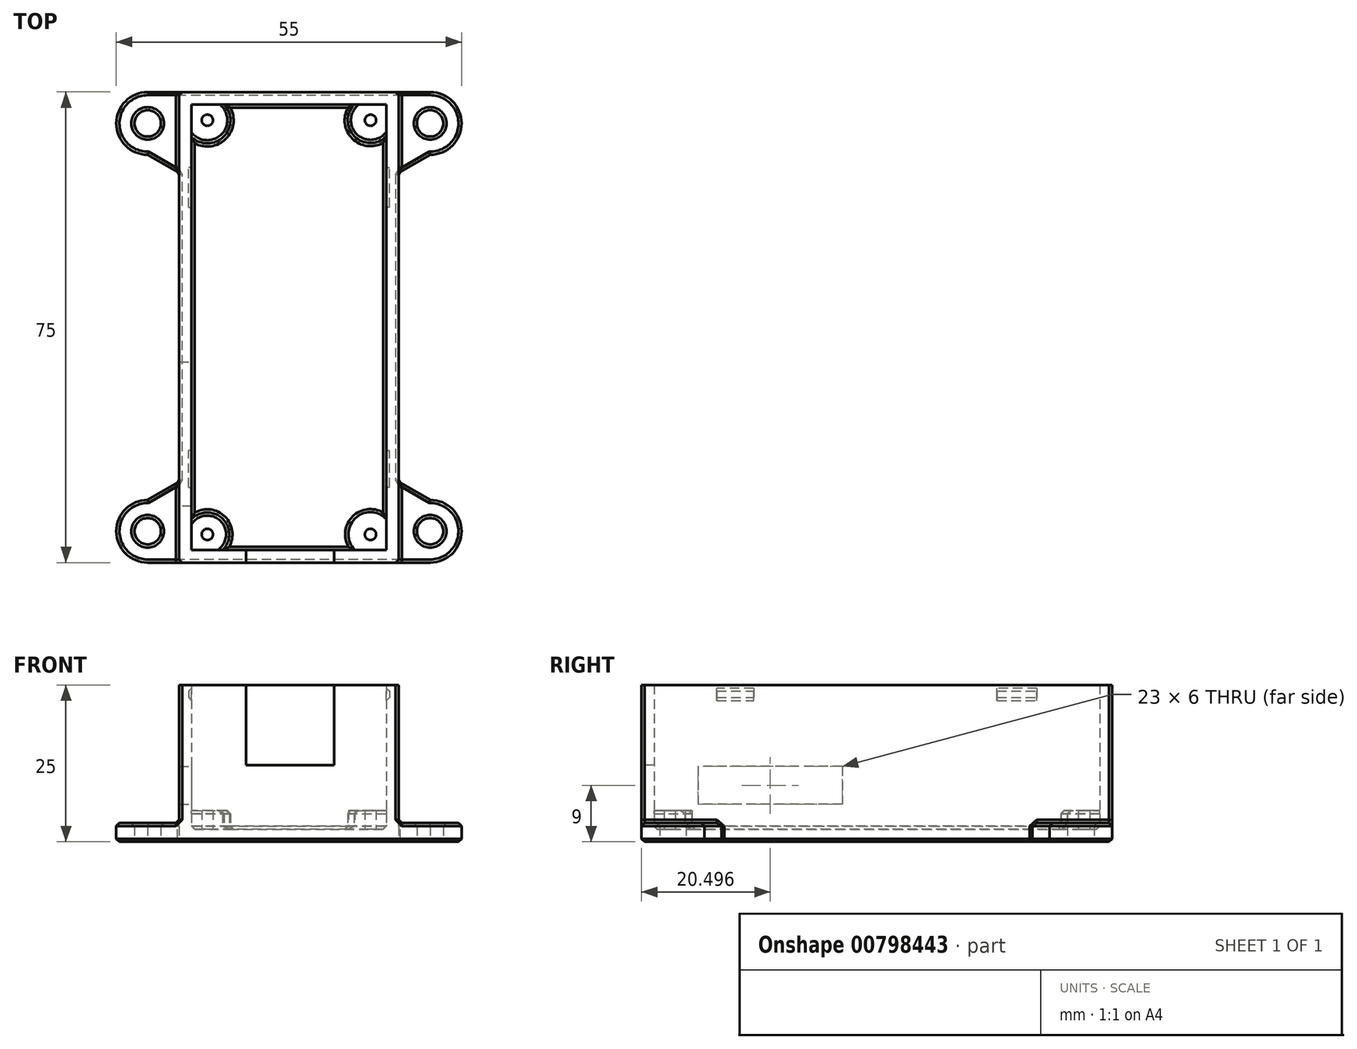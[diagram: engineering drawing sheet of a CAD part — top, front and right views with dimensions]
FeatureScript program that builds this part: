
annotation { "Feature Type Name" : "Feature", "Feature Type Description" : "" }
export const myFeature = defineFeature(function(context is Context, id is Id, definition is map)
    precondition{}
    {
        {
            var Q0;
            Q0=qCreatedBy(makeId("Top.planeOp"),FACE);
            var sketch = newSketch(context, id + "F0", { "sketchPlane" : qUnion([Q0])});
            skLineSegment(sketch, "E0.bottom", {"start": v(-31.58, 41.85) * mm, "end": v(-0.58, 41.85) * mm});
            skLineSegment(sketch, "E0.top", {"start": v(-31.58, -29.15) * mm, "end": v(-0.58, -29.15) * mm});
            skLineSegment(sketch, "E0.left", {"start": v(-31.58, 41.85) * mm, "end": v(-31.58, -29.15) * mm});
            skLineSegment(sketch, "E0.right", {"start": v(-0.58, 41.85) * mm, "end": v(-0.58, -29.15) * mm});
            skCircle(sketch, "E1", {"center": v(-29.08, 39.35) * mm, "radius": 0.9 * mm});
            skCircle(sketch, "E2", {"center": v(-3.08, 39.35) * mm, "radius": 0.9 * mm});
            skCircle(sketch, "E3", {"center": v(-29.08, 39.35) * mm, "radius": 3.69 * mm});
            skCircle(sketch, "E4", {"center": v(-3.08, 39.35) * mm, "radius": 3.62 * mm});
            skCircle(sketch, "E5", {"center": v(-29.08, -26.65) * mm, "radius": 0.9 * mm});
            skCircle(sketch, "E6", {"center": v(-3.08, -26.65) * mm, "radius": 0.9 * mm});
            skCircle(sketch, "E7", {"center": v(-29.08, -26.65) * mm, "radius": 3.5 * mm});
            skCircle(sketch, "E8", {"center": v(-3.08, -26.65) * mm, "radius": 3.54 * mm});
            skLineSegment(sketch, "E9.bottom", {"start": v(-33.58, 43.85) * mm, "end": v(1.42, 43.85) * mm});
            skLineSegment(sketch, "E9.top", {"start": v(-33.58, -31.15) * mm, "end": v(1.42, -31.15) * mm});
            skLineSegment(sketch, "E9.left", {"start": v(-33.58, 43.85) * mm, "end": v(-33.58, -31.15) * mm});
            skLineSegment(sketch, "E9.right", {"start": v(1.42, 43.85) * mm, "end": v(1.42, -31.15) * mm});
            skLineSegment(sketch, "E10.bottom", {"start": v(-32.08, -19.15) * mm, "end": v(-0.08, -19.15) * mm});
            skLineSegment(sketch, "E10.top", {"start": v(-32.08, -13.29) * mm, "end": v(-0.08, -13.29) * mm});
            skLineSegment(sketch, "E10.left", {"start": v(-32.08, -19.15) * mm, "end": v(-32.08, -13.29) * mm});
            skLineSegment(sketch, "E10.right", {"start": v(-0.08, -19.15) * mm, "end": v(-0.08, -13.29) * mm});
            skLineSegment(sketch, "E11.bottom", {"start": v(-32.08, 25.48) * mm, "end": v(-0.08, 25.48) * mm});
            skLineSegment(sketch, "E11.top", {"start": v(-32.08, 31.85) * mm, "end": v(-0.08, 31.85) * mm});
            skLineSegment(sketch, "E11.left", {"start": v(-32.08, 25.48) * mm, "end": v(-32.08, 31.85) * mm});
            skLineSegment(sketch, "E11.right", {"start": v(-0.08, 25.48) * mm, "end": v(-0.08, 31.85) * mm});
            skLineSegment(sketch, "E12.left", {"start": v(-22.9, -29.15) * mm, "end": v(-22.9, -31.15) * mm});
            skLineSegment(sketch, "E12.right", {"start": v(-8.9, -29.15) * mm, "end": v(-8.9, -31.15) * mm});
            skLineSegment(sketch, "E13", {"start": v(1.42, 43.85) * mm, "end": v(6.42, 43.85) * mm});
            skArc(sketch, "E14", {"start": v(6.42, 43.85) * mm, "mid": v(11.42, 38.85) * mm, "end": v(6.42, 33.85) * mm});
            skLineSegment(sketch, "E15", {"start": v(6.42, 33.85) * mm, "end": v(1.42, 30.96) * mm});
            skCircle(sketch, "E16", {"center": v(6.42, 38.85) * mm, "radius": 2.1 * mm});
            skLineSegment(sketch, "E17", {"start": v(-33.58, 43.85) * mm, "end": v(-38.58, 43.85) * mm});
            skArc(sketch, "E18", {"start": v(-38.58, 43.85) * mm, "mid": v(-43.58, 38.85) * mm, "end": v(-38.58, 33.85) * mm});
            skLineSegment(sketch, "E19", {"start": v(-38.58, 33.85) * mm, "end": v(-33.58, 30.96) * mm});
            skLineSegment(sketch, "E20", {"start": v(1.42, -31.15) * mm, "end": v(6.42, -31.15) * mm});
            skArc(sketch, "E21", {"start": v(6.42, -31.15) * mm, "mid": v(11.42, -26.15) * mm, "end": v(6.42, -21.15) * mm});
            skLineSegment(sketch, "E22", {"start": v(6.42, -21.15) * mm, "end": v(1.42, -18.27) * mm});
            skLineSegment(sketch, "E23", {"start": v(-33.58, -31.15) * mm, "end": v(-38.58, -31.15) * mm});
            skArc(sketch, "E24", {"start": v(-38.58, -31.15) * mm, "mid": v(-43.58, -26.15) * mm, "end": v(-38.58, -21.15) * mm});
            skLineSegment(sketch, "E25", {"start": v(-38.58, -21.15) * mm, "end": v(-33.58, -18.27) * mm});
            skCircle(sketch, "E26", {"center": v(-38.58, 38.85) * mm, "radius": 2.1 * mm});
            skCircle(sketch, "E27", {"center": v(-38.58, -26.15) * mm, "radius": 2.1 * mm});
            skCircle(sketch, "E28", {"center": v(6.42, -26.15) * mm, "radius": 2.1 * mm});
            skLineSegment(sketch, "E29", {"start": v(-31.58, -22.15) * mm, "end": v(-33.58, -22.15) * mm});
            skLineSegment(sketch, "E30", {"start": v(-33.58, 0.85) * mm, "end": v(-31.58, 0.85) * mm});
            skSolve(sketch);
        }
        {
            var Q0;
            Q0=makeQuery(id+"F0.imprint","IMPRINT",FACE,{"disambiguationData":[TD([[makeQuery(id+"F0.imprint","IMPRINT",EDGE,{"derivedFrom":sQuery(id+"F0.wireOp",EDGE,"E9.bottom")}),-1.0]])]});
            var Q1;
            {var subQ0=sQuery(id+"F0.wireOp",EDGE,"E0.right");var subQ1=sQuery(id+"F0.wireOp",EDGE,"E0.bottom");var subQ2=makeQuery(id+"F0.imprint","INTERSECT",VERTEX,{"derivedFrom":[subQ1,subQ0]});Q1=makeQuery(id+"F0.imprint","IMPRINT",FACE,{"disambiguationData":[TD([[makeQuery(id+"F0.imprint","IMPRINT",EDGE,{"disambiguationData":[TD([[subQ2,1.0]])],"derivedFrom":subQ1}),1.0]])]});}
            var Q2;
            {var subQ0=sQuery(id+"F0.wireOp",EDGE,"E7");var subQ1=sQuery(id+"F0.wireOp",EDGE,"E0.top");var subQ2=makeQuery(id+"F0.imprint","INTERSECT",VERTEX,{"disambiguationData":[OD(1.0)],"derivedFrom":[subQ1,subQ0]});Q2=makeQuery(id+"F0.imprint","IMPRINT",FACE,{"disambiguationData":[TD([[makeQuery(id+"F0.imprint","IMPRINT",EDGE,{"disambiguationData":[TD([[subQ2,-1.0]])],"derivedFrom":subQ1}),1.0]])]});}
            var Q3;
            {var subQ0=sQuery(id+"F0.wireOp",EDGE,"E12.right");var subQ1=sQuery(id+"F0.wireOp",EDGE,"E0.top");var subQ2=makeQuery(id+"F0.imprint","INTERSECT",VERTEX,{"derivedFrom":[subQ1,subQ0]});Q3=makeQuery(id+"F0.imprint","IMPRINT",FACE,{"disambiguationData":[TD([[makeQuery(id+"F0.imprint","IMPRINT",EDGE,{"disambiguationData":[TD([[subQ2,-1.0]])],"derivedFrom":subQ1}),1.0]])]});}
            var Q4;
            Q4=makeQuery(id+"F0.imprint","IMPRINT",FACE,{"disambiguationData":[TD([[makeQuery(id+"F0.imprint","IMPRINT",EDGE,{"derivedFrom":sQuery(id+"F0.wireOp",EDGE,"E5")}),-1.0]])]});
            var Q5;
            Q5=makeQuery(id+"F0.imprint","IMPRINT",FACE,{"disambiguationData":[TD([[makeQuery(id+"F0.imprint","IMPRINT",EDGE,{"derivedFrom":sQuery(id+"F0.wireOp",EDGE,"E1")}),-1.0]])]});
            var Q6;
            {var subQ0=sQuery(id+"F0.wireOp",EDGE,"E0.left");var subQ1=sQuery(id+"F0.wireOp",EDGE,"E0.bottom");var subQ2=makeQuery(id+"F0.imprint","INTERSECT",VERTEX,{"derivedFrom":[subQ1,subQ0]});Q6=makeQuery(id+"F0.imprint","IMPRINT",FACE,{"disambiguationData":[TD([[makeQuery(id+"F0.imprint","IMPRINT",EDGE,{"disambiguationData":[TD([[subQ2,-1.0]])],"derivedFrom":subQ1}),1.0]])]});}
            var Q7;
            {var subQ0=sQuery(id+"F0.wireOp",EDGE,"E12.left");var subQ1=sQuery(id+"F0.wireOp",EDGE,"E0.top");var subQ2=makeQuery(id+"F0.imprint","INTERSECT",VERTEX,{"derivedFrom":[subQ1,subQ0]});Q7=makeQuery(id+"F0.imprint","IMPRINT",FACE,{"disambiguationData":[TD([[makeQuery(id+"F0.imprint","IMPRINT",EDGE,{"disambiguationData":[TD([[subQ2,-1.0]])],"derivedFrom":subQ1}),-1.0]])]});}
            var Q8;
            {var subQ0=sQuery(id+"F0.wireOp",EDGE,"E11.top");var subQ1=sQuery(id+"F0.wireOp",EDGE,"E0.left");var subQ2=makeQuery(id+"F0.imprint","INTERSECT",VERTEX,{"derivedFrom":[subQ1,subQ0]});Q8=makeQuery(id+"F0.imprint","IMPRINT",FACE,{"disambiguationData":[TD([[makeQuery(id+"F0.imprint","IMPRINT",EDGE,{"disambiguationData":[TD([[subQ2,-1.0]])],"derivedFrom":subQ1}),1.0]])]});}
            var Q9;
            {var subQ3=sQuery(id+"F0.wireOp",EDGE,"E7");var subQ6=sQuery(id+"F0.wireOp",EDGE,"E0.top");var subQ9=makeQuery(id+"F0.imprint","INTERSECT",VERTEX,{"disambiguationData":[OD(1.0)],"derivedFrom":[subQ6,subQ3]});Q9=makeQuery(id+"F0.imprint","IMPRINT",FACE,{"disambiguationData":[TD([[makeQuery(id+"F0.imprint","IMPRINT",EDGE,{"disambiguationData":[TD([[subQ9,-1.0]])],"derivedFrom":subQ6}),-1.0]])]});}
            var Q10;
            Q10=makeQuery(id+"F0.imprint","IMPRINT",FACE,{"disambiguationData":[TD([[makeQuery(id+"F0.imprint","IMPRINT",EDGE,{"derivedFrom":sQuery(id+"F0.wireOp",EDGE,"E2")}),-1.0]])]});
            var Q11;
            {var subQ0=sQuery(id+"F0.wireOp",EDGE,"E10.top");var subQ1=sQuery(id+"F0.wireOp",EDGE,"E0.left");var subQ2=makeQuery(id+"F0.imprint","INTERSECT",VERTEX,{"derivedFrom":[subQ1,subQ0]});Q11=makeQuery(id+"F0.imprint","IMPRINT",FACE,{"disambiguationData":[TD([[makeQuery(id+"F0.imprint","IMPRINT",EDGE,{"disambiguationData":[TD([[subQ2,-1.0]])],"derivedFrom":subQ1}),1.0]])]});}
            var Q12;
            {var subQ5=sQuery(id+"F0.wireOp",EDGE,"E12.bottom");Q12=makeQuery(id+"F0.imprint","IMPRINT",FACE,{"disambiguationData":[TD([[makeQuery(id+"F0.imprint","IMPRINT",EDGE,{"derivedFrom":subQ5}),-1.0]])]});}
            var Q13;
            {var subQ0=sQuery(id+"F0.wireOp",EDGE,"E11.bottom");var subQ1=sQuery(id+"F0.wireOp",EDGE,"E0.left");var subQ2=makeQuery(id+"F0.imprint","INTERSECT",VERTEX,{"derivedFrom":[subQ1,subQ0]});Q13=makeQuery(id+"F0.imprint","IMPRINT",FACE,{"disambiguationData":[TD([[makeQuery(id+"F0.imprint","IMPRINT",EDGE,{"disambiguationData":[TD([[subQ2,-1.0]])],"derivedFrom":subQ1}),1.0]])]});}
            var Q14;
            {var subQ0=sQuery(id+"F0.wireOp",EDGE,"E12.left");var subQ1=sQuery(id+"F0.wireOp",EDGE,"E0.top");var subQ2=makeQuery(id+"F0.imprint","INTERSECT",VERTEX,{"derivedFrom":[subQ1,subQ0]});Q14=makeQuery(id+"F0.imprint","IMPRINT",FACE,{"disambiguationData":[TD([[makeQuery(id+"F0.imprint","IMPRINT",EDGE,{"disambiguationData":[TD([[subQ2,-1.0]])],"derivedFrom":subQ1}),1.0]])]});}
            var Q15;
            Q15=makeQuery(id+"F0.imprint","IMPRINT",FACE,{"disambiguationData":[TD([[makeQuery(id+"F0.imprint","IMPRINT",EDGE,{"derivedFrom":sQuery(id+"F0.wireOp",EDGE,"E6")}),-1.0]])]});
            var Q16;
            {var subQ14=sQuery(id+"F0.wireOp",EDGE,"E12.bottom");Q16=makeQuery(id+"F0.imprint","IMPRINT",FACE,{"disambiguationData":[TD([[makeQuery(id+"F0.imprint","IMPRINT",EDGE,{"derivedFrom":subQ14}),1.0]])]});}
            var Q17;
            {var subQ0=sQuery(id+"F0.wireOp",EDGE,"E3");var subQ1=sQuery(id+"F0.wireOp",EDGE,"E0.bottom");var subQ2=makeQuery(id+"F0.imprint","INTERSECT",VERTEX,{"derivedFrom":[subQ1,subQ0]});Q17=makeQuery(id+"F0.imprint","IMPRINT",FACE,{"disambiguationData":[TD([[makeQuery(id+"F0.imprint","IMPRINT",EDGE,{"disambiguationData":[TD([[subQ2,-1.0]])],"derivedFrom":subQ1}),-1.0]])]});}
            var Q18;
            {var subQ3=sQuery(id+"F0.wireOp",EDGE,"E12.right");var subQ7=sQuery(id+"F0.wireOp",EDGE,"E0.top");var subQ9=makeQuery(id+"F0.imprint","INTERSECT",VERTEX,{"derivedFrom":[subQ7,subQ3]});Q18=makeQuery(id+"F0.imprint","IMPRINT",FACE,{"disambiguationData":[TD([[makeQuery(id+"F0.imprint","IMPRINT",EDGE,{"disambiguationData":[TD([[subQ9,-1.0]])],"derivedFrom":subQ7}),-1.0]])]});}
            var Q19;
            {var subQ0=sQuery(id+"F0.wireOp",EDGE,"E7");var subQ1=sQuery(id+"F0.wireOp",EDGE,"E0.left");var subQ2=makeQuery(id+"F0.imprint","INTERSECT",VERTEX,{"disambiguationData":[OD(0.0)],"derivedFrom":[subQ1,subQ0]});Q19=makeQuery(id+"F0.imprint","IMPRINT",FACE,{"disambiguationData":[TD([[makeQuery(id+"F0.imprint","IMPRINT",EDGE,{"disambiguationData":[TD([[subQ2,-1.0]])],"derivedFrom":subQ1}),-1.0]])]});}
            var Q20;
            {var subQ0=sQuery(id+"F0.wireOp",EDGE,"2mZLKPwa-GTBg-M3pd-c2KF-U8wC3PhsdAiK.left");var subQ1=sQuery(id+"F0.wireOp",EDGE,"E0.top");var subQ2=makeQuery(id+"F0.imprint","INTERSECT",VERTEX,{"derivedFrom":[subQ1,subQ0]});Q20=makeQuery(id+"F0.imprint","IMPRINT",FACE,{"disambiguationData":[TD([[makeQuery(id+"F0.imprint","IMPRINT",EDGE,{"disambiguationData":[TD([[subQ2,-1.0]])],"derivedFrom":subQ1}),1.0]])]});}
            var Q21;
            {var subQ0=sQuery(id+"F0.wireOp",EDGE,"E8");var subQ1=sQuery(id+"F0.wireOp",EDGE,"E0.top");var subQ2=makeQuery(id+"F0.imprint","INTERSECT",VERTEX,{"derivedFrom":[subQ1,subQ0]});Q21=makeQuery(id+"F0.imprint","IMPRINT",FACE,{"disambiguationData":[TD([[makeQuery(id+"F0.imprint","IMPRINT",EDGE,{"disambiguationData":[TD([[subQ2,-1.0]])],"derivedFrom":subQ1}),-1.0]])]});}
            var Q22;
            {var subQ5=sQuery(id+"F0.wireOp",EDGE,"E11.right");Q22=makeQuery(id+"F0.imprint","IMPRINT",FACE,{"disambiguationData":[TD([[makeQuery(id+"F0.imprint","IMPRINT",EDGE,{"derivedFrom":subQ5}),1.0]])]});}
            var Q23;
            {var subQ5=sQuery(id+"F0.wireOp",EDGE,"E10.right");Q23=makeQuery(id+"F0.imprint","IMPRINT",FACE,{"disambiguationData":[TD([[makeQuery(id+"F0.imprint","IMPRINT",EDGE,{"derivedFrom":subQ5}),1.0]])]});}
            var Q24;
            {var subQ5=sQuery(id+"F0.wireOp",EDGE,"E10.left");Q24=makeQuery(id+"F0.imprint","IMPRINT",FACE,{"disambiguationData":[TD([[makeQuery(id+"F0.imprint","IMPRINT",EDGE,{"derivedFrom":subQ5}),-1.0]])]});}
            var Q25;
            {var subQ5=sQuery(id+"F0.wireOp",EDGE,"E11.left");Q25=makeQuery(id+"F0.imprint","IMPRINT",FACE,{"disambiguationData":[TD([[makeQuery(id+"F0.imprint","IMPRINT",EDGE,{"derivedFrom":subQ5}),-1.0]])]});}
            var Q26;
            {var subQ1=sQuery(id+"F0.wireOp",EDGE,"E0.top");var subQ3=sQuery(id+"F0.wireOp",EDGE,"2mZLKPwa-GTBg-M3pd-c2KF-U8wC3PhsdAiK.right");var subQ4=makeQuery(id+"F0.imprint","INTERSECT",VERTEX,{"derivedFrom":[subQ1,subQ3]});Q26=makeQuery(id+"F0.imprint","IMPRINT",FACE,{"disambiguationData":[TD([[makeQuery(id+"F0.imprint","IMPRINT",EDGE,{"disambiguationData":[TD([[subQ4,1.0]])],"derivedFrom":subQ3}),-1.0]])]});}
            var Q27;
            {var subQ0=sQuery(id+"F0.wireOp",EDGE,"E8");var subQ1=sQuery(id+"F0.wireOp",EDGE,"E0.right");var subQ3=makeQuery(id+"F0.imprint","INTERSECT",VERTEX,{"derivedFrom":[subQ1,subQ0]});Q27=makeQuery(id+"F0.imprint","IMPRINT",FACE,{"disambiguationData":[TD([[makeQuery(id+"F0.imprint","IMPRINT",EDGE,{"disambiguationData":[TD([[subQ3,-1.0]])],"derivedFrom":subQ1}),1.0]])]});}
            var Q28;
            {var subQ0=sQuery(id+"F0.wireOp",EDGE,"2mZLKPwa-GTBg-M3pd-c2KF-U8wC3PhsdAiK.left");var subQ1=sQuery(id+"F0.wireOp",EDGE,"E0.top");var subQ2=makeQuery(id+"F0.imprint","INTERSECT",VERTEX,{"derivedFrom":[subQ1,subQ0]});Q28=makeQuery(id+"F0.imprint","IMPRINT",FACE,{"disambiguationData":[TD([[makeQuery(id+"F0.imprint","IMPRINT",EDGE,{"disambiguationData":[TD([[subQ2,-1.0]])],"derivedFrom":subQ1}),-1.0]])]});}
            var Q29;
            {var subQ0=sQuery(id+"F0.wireOp",EDGE,"E8");var subQ1=sQuery(id+"F0.wireOp",EDGE,"E0.top");var subQ2=makeQuery(id+"F0.imprint","INTERSECT",VERTEX,{"derivedFrom":[subQ1,subQ0]});Q29=makeQuery(id+"F0.imprint","IMPRINT",FACE,{"disambiguationData":[TD([[makeQuery(id+"F0.imprint","IMPRINT",EDGE,{"disambiguationData":[TD([[subQ2,-1.0]])],"derivedFrom":subQ1}),1.0]])]});}
            var Q30;
            {var subQ0=sQuery(id+"F0.wireOp",EDGE,"E7");var subQ1=sQuery(id+"F0.wireOp",EDGE,"E0.top");var subQ2=makeQuery(id+"F0.imprint","INTERSECT",VERTEX,{"disambiguationData":[OD(0.0)],"derivedFrom":[subQ1,subQ0]});Q30=makeQuery(id+"F0.imprint","IMPRINT",FACE,{"disambiguationData":[TD([[makeQuery(id+"F0.imprint","IMPRINT",EDGE,{"disambiguationData":[TD([[subQ2,-1.0]])],"derivedFrom":subQ1}),-1.0]])]});}
            var Q31;
            {var subQ0=sQuery(id+"F0.wireOp",EDGE,"E0.left");var subQ1=sQuery(id+"F0.wireOp",EDGE,"E0.top");var subQ2=makeQuery(id+"F0.imprint","INTERSECT",VERTEX,{"derivedFrom":[subQ1,subQ0]});Q31=makeQuery(id+"F0.imprint","IMPRINT",FACE,{"disambiguationData":[TD([[makeQuery(id+"F0.imprint","IMPRINT",EDGE,{"disambiguationData":[TD([[subQ2,-1.0]])],"derivedFrom":subQ1}),1.0]])]});}
            var Q32;
            Q32=makeQuery(id+"F0.imprint","IMPRINT",FACE,{"disambiguationData":[TD([[makeQuery(id+"F0.imprint","IMPRINT",EDGE,{"derivedFrom":sQuery(id+"F0.wireOp",EDGE,"E6")}),1.0]])]});
            var Q33;
            Q33=makeQuery(id+"F0.imprint","IMPRINT",FACE,{"disambiguationData":[TD([[makeQuery(id+"F0.imprint","IMPRINT",EDGE,{"derivedFrom":sQuery(id+"F0.wireOp",EDGE,"E5")}),1.0]])]});
            var Q34;
            Q34=makeQuery(id+"F0.imprint","IMPRINT",FACE,{"disambiguationData":[TD([[makeQuery(id+"F0.imprint","IMPRINT",EDGE,{"derivedFrom":sQuery(id+"F0.wireOp",EDGE,"E2")}),1.0]])]});
            var Q35;
            Q35=makeQuery(id+"F0.imprint","IMPRINT",FACE,{"disambiguationData":[TD([[makeQuery(id+"F0.imprint","IMPRINT",EDGE,{"derivedFrom":sQuery(id+"F0.wireOp",EDGE,"E1")}),1.0]])]});
            var Q36;
            {var subQ0=sQuery(id+"F0.wireOp",EDGE,"2mZLKPwa-GTBg-M3pd-c2KF-U8wC3PhsdAiK.left");var subQ3=sQuery(id+"F0.wireOp",EDGE,"E7");var subQ4=makeQuery(id+"F0.imprint","INTERSECT",VERTEX,{"derivedFrom":[subQ3,subQ0]});Q36=makeQuery(id+"F0.imprint","IMPRINT",FACE,{"disambiguationData":[TD([[makeQuery(id+"F0.imprint","IMPRINT",EDGE,{"disambiguationData":[TD([[subQ4,-1.0]])],"derivedFrom":subQ3}),-1.0]])]});}
            var Q37;
            {var subQ0=sQuery(id+"F0.wireOp",EDGE,"E12.left");var subQ1=sQuery(id+"F0.wireOp",EDGE,"E9.top");var subQ2=makeQuery(id+"F0.imprint","INTERSECT",VERTEX,{"derivedFrom":[subQ1,subQ0]});Q37=makeQuery(id+"F0.imprint","IMPRINT",FACE,{"disambiguationData":[TD([[makeQuery(id+"F0.imprint","IMPRINT",EDGE,{"disambiguationData":[TD([[subQ2,-1.0]])],"derivedFrom":subQ1}),1.0]])]});}
            var Q38;
            {var subQ3=sQuery(id+"F0.wireOp",EDGE,"E8");var subQ7=sQuery(id+"F0.wireOp",EDGE,"2mZLKPwa-GTBg-M3pd-c2KF-U8wC3PhsdAiK.top");var subQ9=makeQuery(id+"F0.imprint","INTERSECT",VERTEX,{"derivedFrom":[subQ3,subQ7]});Q38=makeQuery(id+"F0.imprint","IMPRINT",FACE,{"disambiguationData":[TD([[makeQuery(id+"F0.imprint","IMPRINT",EDGE,{"disambiguationData":[TD([[subQ9,-1.0]])],"derivedFrom":subQ3}),-1.0]])]});}
            var Q39;
            {var subQ0=sQuery(id+"F0.wireOp",EDGE,"2mZLKPwa-GTBg-M3pd-c2KF-U8wC3PhsdAiK.left");var subQ1=sQuery(id+"F0.wireOp",EDGE,"E7");var subQ2=makeQuery(id+"F0.imprint","INTERSECT",VERTEX,{"derivedFrom":[subQ1,subQ0]});Q39=makeQuery(id+"F0.imprint","IMPRINT",FACE,{"disambiguationData":[TD([[makeQuery(id+"F0.imprint","IMPRINT",EDGE,{"disambiguationData":[TD([[subQ2,-1.0]])],"derivedFrom":subQ1}),1.0]])]});}
            var Q40;
            {var subQ0=sQuery(id+"F0.wireOp",EDGE,"2mZLKPwa-GTBg-M3pd-c2KF-U8wC3PhsdAiK.top");var subQ1=sQuery(id+"F0.wireOp",EDGE,"E8");var subQ2=makeQuery(id+"F0.imprint","INTERSECT",VERTEX,{"derivedFrom":[subQ1,subQ0]});Q40=makeQuery(id+"F0.imprint","IMPRINT",FACE,{"disambiguationData":[TD([[makeQuery(id+"F0.imprint","IMPRINT",EDGE,{"disambiguationData":[TD([[subQ2,-1.0]])],"derivedFrom":subQ1}),1.0]])]});}
            var Q41;
            {var subQ7=sQuery(id+"F0.wireOp",EDGE,"E10.left");Q41=makeQuery(id+"F0.imprint","IMPRINT",FACE,{"disambiguationData":[TD([[makeQuery(id+"F0.imprint","IMPRINT",EDGE,{"derivedFrom":subQ7}),1.0]])]});}
            extrude(context, id + "F1", {"entities" : qUnion([Q0, Q1, Q2, Q3, Q4, Q5, Q6, Q7, Q8, Q9, Q10, Q11, Q12, Q13, Q14, Q15, Q16, Q17, Q18, Q19, Q20, Q21, Q22, Q23, Q24, Q25, Q26, Q27, Q28, Q29, Q30, Q31, Q32, Q33, Q34, Q35, Q36, Q37, Q38, Q39, Q40, Q41]), "depth" : 25 * mm, "offsetDistance" : 25 * mm});
        }
        {
            var Q0;
            {var subQ0=sQuery(id+"F0.wireOp",EDGE,"E3");var subQ1=sQuery(id+"F0.wireOp",EDGE,"E0.bottom");var subQ2=makeQuery(id+"F0.imprint","INTERSECT",VERTEX,{"derivedFrom":[subQ1,subQ0]});Q0=makeQuery(id+"F0.imprint","IMPRINT",FACE,{"disambiguationData":[TD([[makeQuery(id+"F0.imprint","IMPRINT",EDGE,{"disambiguationData":[TD([[subQ2,-1.0]])],"derivedFrom":subQ1}),-1.0]])]});}
            var Q1;
            {var subQ0=sQuery(id+"F0.wireOp",EDGE,"E11.top");var subQ1=sQuery(id+"F0.wireOp",EDGE,"E0.left");var subQ2=makeQuery(id+"F0.imprint","INTERSECT",VERTEX,{"derivedFrom":[subQ1,subQ0]});Q1=makeQuery(id+"F0.imprint","IMPRINT",FACE,{"disambiguationData":[TD([[makeQuery(id+"F0.imprint","IMPRINT",EDGE,{"disambiguationData":[TD([[subQ2,-1.0]])],"derivedFrom":subQ1}),1.0]])]});}
            var Q2;
            {var subQ0=sQuery(id+"F0.wireOp",EDGE,"E11.bottom");var subQ1=sQuery(id+"F0.wireOp",EDGE,"E0.left");var subQ2=makeQuery(id+"F0.imprint","INTERSECT",VERTEX,{"derivedFrom":[subQ1,subQ0]});Q2=makeQuery(id+"F0.imprint","IMPRINT",FACE,{"disambiguationData":[TD([[makeQuery(id+"F0.imprint","IMPRINT",EDGE,{"disambiguationData":[TD([[subQ2,-1.0]])],"derivedFrom":subQ1}),1.0]])]});}
            var Q3;
            {var subQ0=sQuery(id+"F0.wireOp",EDGE,"E10.top");var subQ1=sQuery(id+"F0.wireOp",EDGE,"E0.left");var subQ2=makeQuery(id+"F0.imprint","INTERSECT",VERTEX,{"derivedFrom":[subQ1,subQ0]});Q3=makeQuery(id+"F0.imprint","IMPRINT",FACE,{"disambiguationData":[TD([[makeQuery(id+"F0.imprint","IMPRINT",EDGE,{"disambiguationData":[TD([[subQ2,-1.0]])],"derivedFrom":subQ1}),1.0]])]});}
            var Q4;
            {var subQ14=sQuery(id+"F0.wireOp",EDGE,"E12.bottom");Q4=makeQuery(id+"F0.imprint","IMPRINT",FACE,{"disambiguationData":[TD([[makeQuery(id+"F0.imprint","IMPRINT",EDGE,{"derivedFrom":subQ14}),1.0]])]});}
            var Q5;
            {var subQ5=sQuery(id+"F0.wireOp",EDGE,"E12.bottom");Q5=makeQuery(id+"F0.imprint","IMPRINT",FACE,{"disambiguationData":[TD([[makeQuery(id+"F0.imprint","IMPRINT",EDGE,{"derivedFrom":subQ5}),-1.0]])]});}
            var Q6;
            {var subQ0=sQuery(id+"F0.wireOp",EDGE,"E12.left");var subQ1=sQuery(id+"F0.wireOp",EDGE,"E0.top");var subQ2=makeQuery(id+"F0.imprint","INTERSECT",VERTEX,{"derivedFrom":[subQ1,subQ0]});Q6=makeQuery(id+"F0.imprint","IMPRINT",FACE,{"disambiguationData":[TD([[makeQuery(id+"F0.imprint","IMPRINT",EDGE,{"disambiguationData":[TD([[subQ2,-1.0]])],"derivedFrom":subQ1}),1.0]])]});}
            var Q7;
            {var subQ0=sQuery(id+"F0.wireOp",EDGE,"E12.right");var subQ1=sQuery(id+"F0.wireOp",EDGE,"E0.top");var subQ2=makeQuery(id+"F0.imprint","INTERSECT",VERTEX,{"derivedFrom":[subQ1,subQ0]});Q7=makeQuery(id+"F0.imprint","IMPRINT",FACE,{"disambiguationData":[TD([[makeQuery(id+"F0.imprint","IMPRINT",EDGE,{"disambiguationData":[TD([[subQ2,-1.0]])],"derivedFrom":subQ1}),1.0]])]});}
            var Q8;
            Q8=makeQuery(id+"F0.imprint","IMPRINT",FACE,{"disambiguationData":[TD([[makeQuery(id+"F0.imprint","IMPRINT",EDGE,{"derivedFrom":sQuery(id+"F0.wireOp",EDGE,"E6")}),1.0]])]});
            var Q9;
            Q9=makeQuery(id+"F0.imprint","IMPRINT",FACE,{"disambiguationData":[TD([[makeQuery(id+"F0.imprint","IMPRINT",EDGE,{"derivedFrom":sQuery(id+"F0.wireOp",EDGE,"E5")}),1.0]])]});
            var Q10;
            Q10=makeQuery(id+"F0.imprint","IMPRINT",FACE,{"disambiguationData":[TD([[makeQuery(id+"F0.imprint","IMPRINT",EDGE,{"derivedFrom":sQuery(id+"F0.wireOp",EDGE,"E2")}),1.0]])]});
            var Q11;
            Q11=makeQuery(id+"F0.imprint","IMPRINT",FACE,{"disambiguationData":[TD([[makeQuery(id+"F0.imprint","IMPRINT",EDGE,{"derivedFrom":sQuery(id+"F0.wireOp",EDGE,"E1")}),1.0]])]});
            extrude(context, id + "F2", {"entities" : qUnion([Q0, Q1, Q2, Q3, Q4, Q5, Q6, Q7, Q8, Q9, Q10, Q11]), "operationType" : NewBodyOperationType.REMOVE, "depth" : 5 * mm, "offsetDistance" : 25 * mm, "hasSecondDirection" : true, "secondDirectionOppositeDirection" : false, "secondDirectionDepth" : 2 * mm});
        }
        {
            var Q0;
            Q0=makeQuery(id+"F0.imprint","IMPRINT",FACE,{"disambiguationData":[TD([[makeQuery(id+"F0.imprint","IMPRINT",EDGE,{"derivedFrom":sQuery(id+"F0.wireOp",EDGE,"E5")}),-1.0]])]});
            var Q1;
            Q1=makeQuery(id+"F0.imprint","IMPRINT",FACE,{"disambiguationData":[TD([[makeQuery(id+"F0.imprint","IMPRINT",EDGE,{"derivedFrom":sQuery(id+"F0.wireOp",EDGE,"E1")}),-1.0]])]});
            var Q2;
            {var subQ0=sQuery(id+"F0.wireOp",EDGE,"E11.top");var subQ1=sQuery(id+"F0.wireOp",EDGE,"E0.left");var subQ2=makeQuery(id+"F0.imprint","INTERSECT",VERTEX,{"derivedFrom":[subQ1,subQ0]});Q2=makeQuery(id+"F0.imprint","IMPRINT",FACE,{"disambiguationData":[TD([[makeQuery(id+"F0.imprint","IMPRINT",EDGE,{"disambiguationData":[TD([[subQ2,-1.0]])],"derivedFrom":subQ1}),1.0]])]});}
            var Q3;
            Q3=makeQuery(id+"F0.imprint","IMPRINT",FACE,{"disambiguationData":[TD([[makeQuery(id+"F0.imprint","IMPRINT",EDGE,{"derivedFrom":sQuery(id+"F0.wireOp",EDGE,"E2")}),-1.0]])]});
            var Q4;
            {var subQ0=sQuery(id+"F0.wireOp",EDGE,"E10.top");var subQ1=sQuery(id+"F0.wireOp",EDGE,"E0.left");var subQ2=makeQuery(id+"F0.imprint","INTERSECT",VERTEX,{"derivedFrom":[subQ1,subQ0]});Q4=makeQuery(id+"F0.imprint","IMPRINT",FACE,{"disambiguationData":[TD([[makeQuery(id+"F0.imprint","IMPRINT",EDGE,{"disambiguationData":[TD([[subQ2,-1.0]])],"derivedFrom":subQ1}),1.0]])]});}
            var Q5;
            {var subQ5=sQuery(id+"F0.wireOp",EDGE,"E12.bottom");Q5=makeQuery(id+"F0.imprint","IMPRINT",FACE,{"disambiguationData":[TD([[makeQuery(id+"F0.imprint","IMPRINT",EDGE,{"derivedFrom":subQ5}),-1.0]])]});}
            var Q6;
            {var subQ0=sQuery(id+"F0.wireOp",EDGE,"E11.bottom");var subQ1=sQuery(id+"F0.wireOp",EDGE,"E0.left");var subQ2=makeQuery(id+"F0.imprint","INTERSECT",VERTEX,{"derivedFrom":[subQ1,subQ0]});Q6=makeQuery(id+"F0.imprint","IMPRINT",FACE,{"disambiguationData":[TD([[makeQuery(id+"F0.imprint","IMPRINT",EDGE,{"disambiguationData":[TD([[subQ2,-1.0]])],"derivedFrom":subQ1}),1.0]])]});}
            var Q7;
            Q7=makeQuery(id+"F0.imprint","IMPRINT",FACE,{"disambiguationData":[TD([[makeQuery(id+"F0.imprint","IMPRINT",EDGE,{"derivedFrom":sQuery(id+"F0.wireOp",EDGE,"E6")}),-1.0]])]});
            var Q8;
            {var subQ14=sQuery(id+"F0.wireOp",EDGE,"E12.bottom");Q8=makeQuery(id+"F0.imprint","IMPRINT",FACE,{"disambiguationData":[TD([[makeQuery(id+"F0.imprint","IMPRINT",EDGE,{"derivedFrom":subQ14}),1.0]])]});}
            var Q9;
            {var subQ0=sQuery(id+"F0.wireOp",EDGE,"E3");var subQ1=sQuery(id+"F0.wireOp",EDGE,"E0.bottom");var subQ2=makeQuery(id+"F0.imprint","INTERSECT",VERTEX,{"derivedFrom":[subQ1,subQ0]});Q9=makeQuery(id+"F0.imprint","IMPRINT",FACE,{"disambiguationData":[TD([[makeQuery(id+"F0.imprint","IMPRINT",EDGE,{"disambiguationData":[TD([[subQ2,-1.0]])],"derivedFrom":subQ1}),-1.0]])]});}
            var Q10;
            {var subQ0=sQuery(id+"F0.wireOp",EDGE,"E7");var subQ1=sQuery(id+"F0.wireOp",EDGE,"E0.top");var subQ2=makeQuery(id+"F0.imprint","INTERSECT",VERTEX,{"disambiguationData":[OD(1.0)],"derivedFrom":[subQ1,subQ0]});Q10=makeQuery(id+"F0.imprint","IMPRINT",FACE,{"disambiguationData":[TD([[makeQuery(id+"F0.imprint","IMPRINT",EDGE,{"disambiguationData":[TD([[subQ2,-1.0]])],"derivedFrom":subQ1}),1.0]])]});}
            var Q11;
            {var subQ0=sQuery(id+"F0.wireOp",EDGE,"E12.right");var subQ1=sQuery(id+"F0.wireOp",EDGE,"E0.top");var subQ2=makeQuery(id+"F0.imprint","INTERSECT",VERTEX,{"derivedFrom":[subQ1,subQ0]});Q11=makeQuery(id+"F0.imprint","IMPRINT",FACE,{"disambiguationData":[TD([[makeQuery(id+"F0.imprint","IMPRINT",EDGE,{"disambiguationData":[TD([[subQ2,-1.0]])],"derivedFrom":subQ1}),1.0]])]});}
            var Q12;
            {var subQ0=sQuery(id+"F0.wireOp",EDGE,"E12.left");var subQ1=sQuery(id+"F0.wireOp",EDGE,"E0.top");var subQ2=makeQuery(id+"F0.imprint","INTERSECT",VERTEX,{"derivedFrom":[subQ1,subQ0]});Q12=makeQuery(id+"F0.imprint","IMPRINT",FACE,{"disambiguationData":[TD([[makeQuery(id+"F0.imprint","IMPRINT",EDGE,{"disambiguationData":[TD([[subQ2,-1.0]])],"derivedFrom":subQ1}),1.0]])]});}
            var Q13;
            {var subQ0=sQuery(id+"F0.wireOp",EDGE,"E8");var subQ1=sQuery(id+"F0.wireOp",EDGE,"E0.top");var subQ2=makeQuery(id+"F0.imprint","INTERSECT",VERTEX,{"derivedFrom":[subQ1,subQ0]});Q13=makeQuery(id+"F0.imprint","IMPRINT",FACE,{"disambiguationData":[TD([[makeQuery(id+"F0.imprint","IMPRINT",EDGE,{"disambiguationData":[TD([[subQ2,-1.0]])],"derivedFrom":subQ1}),1.0]])]});}
            var Q14;
            {var subQ0=sQuery(id+"F0.wireOp",EDGE,"2mZLKPwa-GTBg-M3pd-c2KF-U8wC3PhsdAiK.left");var subQ1=sQuery(id+"F0.wireOp",EDGE,"E0.top");var subQ2=makeQuery(id+"F0.imprint","INTERSECT",VERTEX,{"derivedFrom":[subQ1,subQ0]});Q14=makeQuery(id+"F0.imprint","IMPRINT",FACE,{"disambiguationData":[TD([[makeQuery(id+"F0.imprint","IMPRINT",EDGE,{"disambiguationData":[TD([[subQ2,-1.0]])],"derivedFrom":subQ1}),1.0]])]});}
            var Q15;
            {var subQ0=sQuery(id+"F0.wireOp",EDGE,"E0.left");var subQ1=sQuery(id+"F0.wireOp",EDGE,"E0.top");var subQ2=makeQuery(id+"F0.imprint","INTERSECT",VERTEX,{"derivedFrom":[subQ1,subQ0]});Q15=makeQuery(id+"F0.imprint","IMPRINT",FACE,{"disambiguationData":[TD([[makeQuery(id+"F0.imprint","IMPRINT",EDGE,{"disambiguationData":[TD([[subQ2,-1.0]])],"derivedFrom":subQ1}),1.0]])]});}
            var Q16;
            Q16=makeQuery(id+"F0.imprint","IMPRINT",FACE,{"disambiguationData":[TD([[makeQuery(id+"F0.imprint","IMPRINT",EDGE,{"derivedFrom":sQuery(id+"F0.wireOp",EDGE,"E6")}),1.0]])]});
            var Q17;
            Q17=makeQuery(id+"F0.imprint","IMPRINT",FACE,{"disambiguationData":[TD([[makeQuery(id+"F0.imprint","IMPRINT",EDGE,{"derivedFrom":sQuery(id+"F0.wireOp",EDGE,"E5")}),1.0]])]});
            var Q18;
            Q18=makeQuery(id+"F0.imprint","IMPRINT",FACE,{"disambiguationData":[TD([[makeQuery(id+"F0.imprint","IMPRINT",EDGE,{"derivedFrom":sQuery(id+"F0.wireOp",EDGE,"E2")}),1.0]])]});
            var Q19;
            Q19=makeQuery(id+"F0.imprint","IMPRINT",FACE,{"disambiguationData":[TD([[makeQuery(id+"F0.imprint","IMPRINT",EDGE,{"derivedFrom":sQuery(id+"F0.wireOp",EDGE,"E1")}),1.0]])]});
            extrude(context, id + "F3", {"entities" : qUnion([Q0, Q1, Q2, Q3, Q4, Q5, Q6, Q7, Q8, Q9, Q10, Q11, Q12, Q13, Q14, Q15, Q16, Q17, Q18, Q19]), "operationType" : NewBodyOperationType.REMOVE, "depth" : 25 * mm, "offsetDistance" : 25 * mm, "hasSecondDirection" : true, "secondDirectionOppositeDirection" : false, "secondDirectionDepth" : 5 * mm});
        }
        {
            var Q0;
            {var subQ7=sQuery(id+"F0.wireOp",EDGE,"E10.left");Q0=makeQuery(id+"F0.imprint","IMPRINT",FACE,{"disambiguationData":[TD([[makeQuery(id+"F0.imprint","IMPRINT",EDGE,{"derivedFrom":subQ7}),1.0]])]});}
            var Q1;
            {var subQ5=sQuery(id+"F0.wireOp",EDGE,"E10.left");Q1=makeQuery(id+"F0.imprint","IMPRINT",FACE,{"disambiguationData":[TD([[makeQuery(id+"F0.imprint","IMPRINT",EDGE,{"derivedFrom":subQ5}),-1.0]])]});}
            extrude(context, id + "F4", {"entities" : qUnion([Q0, Q1]), "operationType" : NewBodyOperationType.REMOVE, "depth" : 12 * mm, "offsetDistance" : 25 * mm, "hasSecondDirection" : true, "secondDirectionOppositeDirection" : false, "secondDirectionDepth" : 6 * mm});
        }
        {
            var Q0;
            {var subQ0=sQuery(id+"F0.wireOp",EDGE,"E12.left");var subQ1=sQuery(id+"F0.wireOp",EDGE,"E9.top");var subQ2=makeQuery(id+"F0.imprint","INTERSECT",VERTEX,{"derivedFrom":[subQ1,subQ0]});Q0=makeQuery(id+"F0.imprint","IMPRINT",FACE,{"disambiguationData":[TD([[makeQuery(id+"F0.imprint","IMPRINT",EDGE,{"disambiguationData":[TD([[subQ2,-1.0]])],"derivedFrom":subQ1}),-1.0]])]});}
            var Q1;
            {var subQ0=sQuery(id+"F0.wireOp",EDGE,"E12.left");var subQ1=sQuery(id+"F0.wireOp",EDGE,"E9.top");var subQ2=makeQuery(id+"F0.imprint","INTERSECT",VERTEX,{"derivedFrom":[subQ1,subQ0]});Q1=makeQuery(id+"F0.imprint","IMPRINT",FACE,{"disambiguationData":[TD([[makeQuery(id+"F0.imprint","IMPRINT",EDGE,{"disambiguationData":[TD([[subQ2,-1.0]])],"derivedFrom":subQ1}),1.0]])]});}
            extrude(context, id + "F5", {"entities" : qUnion([Q0, Q1]), "operationType" : NewBodyOperationType.REMOVE, "depth" : 25 * mm, "offsetDistance" : 25 * mm, "hasSecondDirection" : true, "secondDirectionOppositeDirection" : false, "secondDirectionDepth" : 12.2 * mm});
        }
        {
            var Q0;
            {var subQ0=sQuery(id+"F0.wireOp",EDGE,"E11.top");var subQ1=sQuery(id+"F0.wireOp",EDGE,"E0.left");var subQ2=makeQuery(id+"F0.imprint","INTERSECT",VERTEX,{"derivedFrom":[subQ1,subQ0]});Q0=makeQuery(id+"F0.imprint","IMPRINT",FACE,{"disambiguationData":[TD([[makeQuery(id+"F0.imprint","IMPRINT",EDGE,{"disambiguationData":[TD([[subQ2,-1.0]])],"derivedFrom":subQ1}),1.0]])]});}
            var Q1;
            {var subQ5=sQuery(id+"F0.wireOp",EDGE,"E11.left");Q1=makeQuery(id+"F0.imprint","IMPRINT",FACE,{"disambiguationData":[TD([[makeQuery(id+"F0.imprint","IMPRINT",EDGE,{"derivedFrom":subQ5}),-1.0]])]});}
            var Q2;
            {var subQ5=sQuery(id+"F0.wireOp",EDGE,"E11.right");Q2=makeQuery(id+"F0.imprint","IMPRINT",FACE,{"disambiguationData":[TD([[makeQuery(id+"F0.imprint","IMPRINT",EDGE,{"derivedFrom":subQ5}),1.0]])]});}
            var Q3;
            {var subQ5=sQuery(id+"F0.wireOp",EDGE,"E10.right");Q3=makeQuery(id+"F0.imprint","IMPRINT",FACE,{"disambiguationData":[TD([[makeQuery(id+"F0.imprint","IMPRINT",EDGE,{"derivedFrom":subQ5}),1.0]])]});}
            var Q4;
            {var subQ0=sQuery(id+"F0.wireOp",EDGE,"E10.top");var subQ1=sQuery(id+"F0.wireOp",EDGE,"E0.left");var subQ2=makeQuery(id+"F0.imprint","INTERSECT",VERTEX,{"derivedFrom":[subQ1,subQ0]});Q4=makeQuery(id+"F0.imprint","IMPRINT",FACE,{"disambiguationData":[TD([[makeQuery(id+"F0.imprint","IMPRINT",EDGE,{"disambiguationData":[TD([[subQ2,-1.0]])],"derivedFrom":subQ1}),1.0]])]});}
            var Q5;
            {var subQ5=sQuery(id+"F0.wireOp",EDGE,"E10.left");Q5=makeQuery(id+"F0.imprint","IMPRINT",FACE,{"disambiguationData":[TD([[makeQuery(id+"F0.imprint","IMPRINT",EDGE,{"derivedFrom":subQ5}),-1.0]])]});}
            extrude(context, id + "F6", {"entities" : qUnion([Q0, Q1, Q2, Q3, Q4, Q5]), "operationType" : NewBodyOperationType.REMOVE, "depth" : 24 * mm, "offsetDistance" : 25 * mm, "hasSecondDirection" : true, "secondDirectionOppositeDirection" : false, "secondDirectionDepth" : 23 * mm});
        }
        {
            var Q0;
            {var subQ1=sQuery(id+"F0.wireOp",EDGE,"E17");Q0=makeQuery(id+"F0.imprint","IMPRINT",FACE,{"disambiguationData":[TD([[makeQuery(id+"F0.imprint","IMPRINT",EDGE,{"derivedFrom":subQ1}),1.0]])]});}
            var Q1;
            {var subQ1=sQuery(id+"F0.wireOp",EDGE,"E13");Q1=makeQuery(id+"F0.imprint","IMPRINT",FACE,{"disambiguationData":[TD([[makeQuery(id+"F0.imprint","IMPRINT",EDGE,{"derivedFrom":subQ1}),-1.0]])]});}
            var Q2;
            {var subQ1=sQuery(id+"F0.wireOp",EDGE,"E20");Q2=makeQuery(id+"F0.imprint","IMPRINT",FACE,{"disambiguationData":[TD([[makeQuery(id+"F0.imprint","IMPRINT",EDGE,{"derivedFrom":subQ1}),1.0]])]});}
            var Q3;
            {var subQ1=sQuery(id+"F0.wireOp",EDGE,"E23");Q3=makeQuery(id+"F0.imprint","IMPRINT",FACE,{"disambiguationData":[TD([[makeQuery(id+"F0.imprint","IMPRINT",EDGE,{"derivedFrom":subQ1}),-1.0]])]});}
            extrude(context, id + "F7", {"entities" : qUnion([Q0, Q1, Q2, Q3]), "operationType" : NewBodyOperationType.ADD, "depth" : 3 * mm, "offsetDistance" : 25 * mm});
        }
        {
            var Q0;
            {var subQ0=sQuery(id+"F0.wireOp",EDGE,"E11.top");var subQ1=sQuery(id+"F0.wireOp",EDGE,"E11.bottom");var subQ2=sQuery(id+"F0.wireOp",EDGE,"E0.left");var subQ4=makeQuery(id+"F0.imprint","INTERSECT",VERTEX,{"derivedFrom":[subQ2,sQuery(id+"F0.wireOp",EDGE,"E10.bottom")]});var subQ5=makeQuery(id+"F0.imprint","INTERSECT",VERTEX,{"derivedFrom":[subQ2,sQuery(id+"F0.wireOp",EDGE,"E10.top")]});var subQ6=makeQuery(id+"F0.imprint","INTERSECT",VERTEX,{"derivedFrom":[subQ2,subQ1]});var subQ7=makeQuery(id+"F0.imprint","INTERSECT",VERTEX,{"derivedFrom":[subQ2,subQ0]});Q0=makeQuery(id+"F6.boolean.opBoolean","INTERSECT",EDGE,{"derivedFrom":[makeQuery(id+"F3.boolean.opBoolean","MERGE",FACE,{"derivedFrom":[makeQuery(id+"F2.boolean.opBoolean","COPY",FACE,{"derivedFrom":makeQuery(id+"F2.opExtrude","SWEPT_FACE",FACE,{"disambiguationData":[OSD([subQ2]),TDD([makeQuery(id+"F0.imprint","IMPRINT",EDGE,{"disambiguationData":[TD([[makeQuery(id+"F0.imprint","INTERSECT",VERTEX,{"derivedFrom":[subQ2,sQuery(id+"F0.wireOp",EDGE,"E3")]}),-1.0]])],"derivedFrom":subQ2}),makeQuery(id+"F0.imprint","IMPRINT",EDGE,{"disambiguationData":[TD([[subQ7,-1.0]])],"derivedFrom":subQ2}),makeQuery(id+"F0.imprint","IMPRINT",EDGE,{"disambiguationData":[TD([[subQ6,-1.0]])],"derivedFrom":subQ2}),makeQuery(id+"F0.imprint","IMPRINT",EDGE,{"disambiguationData":[TD([[subQ5,-1.0]])],"derivedFrom":subQ2}),makeQuery(id+"F0.imprint","IMPRINT",EDGE,{"disambiguationData":[TD([[subQ4,-1.0]])],"derivedFrom":subQ2})])]})}),makeQuery(id+"F2.boolean.opBoolean","COPY",FACE,{"derivedFrom":makeQuery(id+"F2.opExtrude","SWEPT_FACE",FACE,{"disambiguationData":[OSD([subQ2]),TDD([makeQuery(id+"F0.imprint","IMPRINT",EDGE,{"disambiguationData":[TD([[makeQuery(id+"F0.imprint","INTERSECT",VERTEX,{"derivedFrom":[sQuery(id+"F0.wireOp",EDGE,"E0.top"),subQ2]}),1.0]])],"derivedFrom":subQ2})])]})}),makeQuery(id+"F3.opExtrude","SWEPT_FACE",FACE,{"disambiguationData":[OSD([subQ2])]})]}),makeQuery(id+"F6.opExtrude","CAP_FACE",FACE,{"disambiguationData":[OSD([subQ1,subQ0,sQuery(id+"F0.wireOp",EDGE,"E11.left"),sQuery(id+"F0.wireOp",EDGE,"E11.right")])],"isStart":false})]});}
            var Q1;
            {var subQ0=sQuery(id+"F0.wireOp",EDGE,"E10.top");var subQ1=sQuery(id+"F0.wireOp",EDGE,"E10.bottom");var subQ2=sQuery(id+"F0.wireOp",EDGE,"E0.left");var subQ4=makeQuery(id+"F0.imprint","INTERSECT",VERTEX,{"derivedFrom":[subQ2,subQ1]});var subQ5=makeQuery(id+"F0.imprint","INTERSECT",VERTEX,{"derivedFrom":[subQ2,subQ0]});var subQ6=makeQuery(id+"F0.imprint","INTERSECT",VERTEX,{"derivedFrom":[subQ2,sQuery(id+"F0.wireOp",EDGE,"E11.bottom")]});var subQ7=makeQuery(id+"F0.imprint","INTERSECT",VERTEX,{"derivedFrom":[subQ2,sQuery(id+"F0.wireOp",EDGE,"E11.top")]});Q1=makeQuery(id+"F6.boolean.opBoolean","INTERSECT",EDGE,{"derivedFrom":[makeQuery(id+"F3.boolean.opBoolean","MERGE",FACE,{"derivedFrom":[makeQuery(id+"F2.boolean.opBoolean","COPY",FACE,{"derivedFrom":makeQuery(id+"F2.opExtrude","SWEPT_FACE",FACE,{"disambiguationData":[OSD([subQ2]),TDD([makeQuery(id+"F0.imprint","IMPRINT",EDGE,{"disambiguationData":[TD([[makeQuery(id+"F0.imprint","INTERSECT",VERTEX,{"derivedFrom":[subQ2,sQuery(id+"F0.wireOp",EDGE,"E3")]}),-1.0]])],"derivedFrom":subQ2}),makeQuery(id+"F0.imprint","IMPRINT",EDGE,{"disambiguationData":[TD([[subQ7,-1.0]])],"derivedFrom":subQ2}),makeQuery(id+"F0.imprint","IMPRINT",EDGE,{"disambiguationData":[TD([[subQ6,-1.0]])],"derivedFrom":subQ2}),makeQuery(id+"F0.imprint","IMPRINT",EDGE,{"disambiguationData":[TD([[subQ5,-1.0]])],"derivedFrom":subQ2}),makeQuery(id+"F0.imprint","IMPRINT",EDGE,{"disambiguationData":[TD([[subQ4,-1.0]])],"derivedFrom":subQ2})])]})}),makeQuery(id+"F2.boolean.opBoolean","COPY",FACE,{"derivedFrom":makeQuery(id+"F2.opExtrude","SWEPT_FACE",FACE,{"disambiguationData":[OSD([subQ2]),TDD([makeQuery(id+"F0.imprint","IMPRINT",EDGE,{"disambiguationData":[TD([[makeQuery(id+"F0.imprint","INTERSECT",VERTEX,{"derivedFrom":[sQuery(id+"F0.wireOp",EDGE,"E0.top"),subQ2]}),1.0]])],"derivedFrom":subQ2})])]})}),makeQuery(id+"F3.opExtrude","SWEPT_FACE",FACE,{"disambiguationData":[OSD([subQ2])]})]}),makeQuery(id+"F6.opExtrude","CAP_FACE",FACE,{"disambiguationData":[OSD([subQ1,subQ0,sQuery(id+"F0.wireOp",EDGE,"E10.left"),sQuery(id+"F0.wireOp",EDGE,"E10.right")])],"isStart":false})]});}
            var Q2;
            {var subQ0=sQuery(id+"F0.wireOp",EDGE,"E0.right");Q2=makeQuery(id+"F6.boolean.opBoolean","INTERSECT",EDGE,{"derivedFrom":[makeQuery(id+"F3.boolean.opBoolean","MERGE",FACE,{"derivedFrom":[makeQuery(id+"F2.boolean.opBoolean","COPY",FACE,{"derivedFrom":makeQuery(id+"F2.opExtrude","SWEPT_FACE",FACE,{"disambiguationData":[OSD([subQ0])]})}),makeQuery(id+"F3.opExtrude","SWEPT_FACE",FACE,{"disambiguationData":[OSD([subQ0])]})]}),makeQuery(id+"F6.opExtrude","CAP_FACE",FACE,{"disambiguationData":[OSD([sQuery(id+"F0.wireOp",EDGE,"E11.bottom"),sQuery(id+"F0.wireOp",EDGE,"E11.top"),sQuery(id+"F0.wireOp",EDGE,"E11.left"),sQuery(id+"F0.wireOp",EDGE,"E11.right")])],"isStart":false})]});}
            var Q3;
            {var subQ0=sQuery(id+"F0.wireOp",EDGE,"E0.right");Q3=makeQuery(id+"F6.boolean.opBoolean","INTERSECT",EDGE,{"derivedFrom":[makeQuery(id+"F3.boolean.opBoolean","MERGE",FACE,{"derivedFrom":[makeQuery(id+"F2.boolean.opBoolean","COPY",FACE,{"derivedFrom":makeQuery(id+"F2.opExtrude","SWEPT_FACE",FACE,{"disambiguationData":[OSD([subQ0])]})}),makeQuery(id+"F3.opExtrude","SWEPT_FACE",FACE,{"disambiguationData":[OSD([subQ0])]})]}),makeQuery(id+"F6.opExtrude","CAP_FACE",FACE,{"disambiguationData":[OSD([sQuery(id+"F0.wireOp",EDGE,"E10.bottom"),sQuery(id+"F0.wireOp",EDGE,"E10.top"),sQuery(id+"F0.wireOp",EDGE,"E10.left"),sQuery(id+"F0.wireOp",EDGE,"E10.right")])],"isStart":false})]});}
            var Q4;
            {var subQ0=sQuery(id+"F0.wireOp",EDGE,"E0.right");Q4=makeQuery(id+"F6.boolean.opBoolean","INTERSECT",EDGE,{"derivedFrom":[makeQuery(id+"F3.boolean.opBoolean","MERGE",FACE,{"derivedFrom":[makeQuery(id+"F2.boolean.opBoolean","COPY",FACE,{"derivedFrom":makeQuery(id+"F2.opExtrude","SWEPT_FACE",FACE,{"disambiguationData":[OSD([subQ0])]})}),makeQuery(id+"F3.opExtrude","SWEPT_FACE",FACE,{"disambiguationData":[OSD([subQ0])]})]}),makeQuery(id+"F6.opExtrude","CAP_FACE",FACE,{"disambiguationData":[OSD([sQuery(id+"F0.wireOp",EDGE,"E11.bottom"),sQuery(id+"F0.wireOp",EDGE,"E11.top"),sQuery(id+"F0.wireOp",EDGE,"E11.left"),sQuery(id+"F0.wireOp",EDGE,"E11.right")])],"isStart":true})]});}
            var Q5;
            {var subQ0=sQuery(id+"F0.wireOp",EDGE,"E0.right");Q5=makeQuery(id+"F6.boolean.opBoolean","INTERSECT",EDGE,{"derivedFrom":[makeQuery(id+"F3.boolean.opBoolean","MERGE",FACE,{"derivedFrom":[makeQuery(id+"F2.boolean.opBoolean","COPY",FACE,{"derivedFrom":makeQuery(id+"F2.opExtrude","SWEPT_FACE",FACE,{"disambiguationData":[OSD([subQ0])]})}),makeQuery(id+"F3.opExtrude","SWEPT_FACE",FACE,{"disambiguationData":[OSD([subQ0])]})]}),makeQuery(id+"F6.opExtrude","CAP_FACE",FACE,{"disambiguationData":[OSD([sQuery(id+"F0.wireOp",EDGE,"E10.bottom"),sQuery(id+"F0.wireOp",EDGE,"E10.top"),sQuery(id+"F0.wireOp",EDGE,"E10.left"),sQuery(id+"F0.wireOp",EDGE,"E10.right")])],"isStart":true})]});}
            var Q6;
            {var subQ0=sQuery(id+"F0.wireOp",EDGE,"E10.top");var subQ1=sQuery(id+"F0.wireOp",EDGE,"E10.bottom");var subQ2=sQuery(id+"F0.wireOp",EDGE,"E0.left");var subQ4=makeQuery(id+"F0.imprint","INTERSECT",VERTEX,{"derivedFrom":[subQ2,subQ1]});var subQ5=makeQuery(id+"F0.imprint","INTERSECT",VERTEX,{"derivedFrom":[subQ2,subQ0]});var subQ6=makeQuery(id+"F0.imprint","INTERSECT",VERTEX,{"derivedFrom":[subQ2,sQuery(id+"F0.wireOp",EDGE,"E11.bottom")]});var subQ7=makeQuery(id+"F0.imprint","INTERSECT",VERTEX,{"derivedFrom":[subQ2,sQuery(id+"F0.wireOp",EDGE,"E11.top")]});Q6=makeQuery(id+"F6.boolean.opBoolean","INTERSECT",EDGE,{"derivedFrom":[makeQuery(id+"F3.boolean.opBoolean","MERGE",FACE,{"derivedFrom":[makeQuery(id+"F2.boolean.opBoolean","COPY",FACE,{"derivedFrom":makeQuery(id+"F2.opExtrude","SWEPT_FACE",FACE,{"disambiguationData":[OSD([subQ2]),TDD([makeQuery(id+"F0.imprint","IMPRINT",EDGE,{"disambiguationData":[TD([[makeQuery(id+"F0.imprint","INTERSECT",VERTEX,{"derivedFrom":[subQ2,sQuery(id+"F0.wireOp",EDGE,"E3")]}),-1.0]])],"derivedFrom":subQ2}),makeQuery(id+"F0.imprint","IMPRINT",EDGE,{"disambiguationData":[TD([[subQ7,-1.0]])],"derivedFrom":subQ2}),makeQuery(id+"F0.imprint","IMPRINT",EDGE,{"disambiguationData":[TD([[subQ6,-1.0]])],"derivedFrom":subQ2}),makeQuery(id+"F0.imprint","IMPRINT",EDGE,{"disambiguationData":[TD([[subQ5,-1.0]])],"derivedFrom":subQ2}),makeQuery(id+"F0.imprint","IMPRINT",EDGE,{"disambiguationData":[TD([[subQ4,-1.0]])],"derivedFrom":subQ2})])]})}),makeQuery(id+"F2.boolean.opBoolean","COPY",FACE,{"derivedFrom":makeQuery(id+"F2.opExtrude","SWEPT_FACE",FACE,{"disambiguationData":[OSD([subQ2]),TDD([makeQuery(id+"F0.imprint","IMPRINT",EDGE,{"disambiguationData":[TD([[makeQuery(id+"F0.imprint","INTERSECT",VERTEX,{"derivedFrom":[sQuery(id+"F0.wireOp",EDGE,"E0.top"),subQ2]}),1.0]])],"derivedFrom":subQ2})])]})}),makeQuery(id+"F3.opExtrude","SWEPT_FACE",FACE,{"disambiguationData":[OSD([subQ2])]})]}),makeQuery(id+"F6.opExtrude","CAP_FACE",FACE,{"disambiguationData":[OSD([subQ1,subQ0,sQuery(id+"F0.wireOp",EDGE,"E10.left"),sQuery(id+"F0.wireOp",EDGE,"E10.right")])],"isStart":true})]});}
            var Q7;
            {var subQ0=sQuery(id+"F0.wireOp",EDGE,"E11.top");var subQ1=sQuery(id+"F0.wireOp",EDGE,"E11.bottom");var subQ2=sQuery(id+"F0.wireOp",EDGE,"E0.left");var subQ4=makeQuery(id+"F0.imprint","INTERSECT",VERTEX,{"derivedFrom":[subQ2,sQuery(id+"F0.wireOp",EDGE,"E10.bottom")]});var subQ5=makeQuery(id+"F0.imprint","INTERSECT",VERTEX,{"derivedFrom":[subQ2,sQuery(id+"F0.wireOp",EDGE,"E10.top")]});var subQ6=makeQuery(id+"F0.imprint","INTERSECT",VERTEX,{"derivedFrom":[subQ2,subQ1]});var subQ7=makeQuery(id+"F0.imprint","INTERSECT",VERTEX,{"derivedFrom":[subQ2,subQ0]});Q7=makeQuery(id+"F6.boolean.opBoolean","INTERSECT",EDGE,{"derivedFrom":[makeQuery(id+"F3.boolean.opBoolean","MERGE",FACE,{"derivedFrom":[makeQuery(id+"F2.boolean.opBoolean","COPY",FACE,{"derivedFrom":makeQuery(id+"F2.opExtrude","SWEPT_FACE",FACE,{"disambiguationData":[OSD([subQ2]),TDD([makeQuery(id+"F0.imprint","IMPRINT",EDGE,{"disambiguationData":[TD([[makeQuery(id+"F0.imprint","INTERSECT",VERTEX,{"derivedFrom":[subQ2,sQuery(id+"F0.wireOp",EDGE,"E3")]}),-1.0]])],"derivedFrom":subQ2}),makeQuery(id+"F0.imprint","IMPRINT",EDGE,{"disambiguationData":[TD([[subQ7,-1.0]])],"derivedFrom":subQ2}),makeQuery(id+"F0.imprint","IMPRINT",EDGE,{"disambiguationData":[TD([[subQ6,-1.0]])],"derivedFrom":subQ2}),makeQuery(id+"F0.imprint","IMPRINT",EDGE,{"disambiguationData":[TD([[subQ5,-1.0]])],"derivedFrom":subQ2}),makeQuery(id+"F0.imprint","IMPRINT",EDGE,{"disambiguationData":[TD([[subQ4,-1.0]])],"derivedFrom":subQ2})])]})}),makeQuery(id+"F2.boolean.opBoolean","COPY",FACE,{"derivedFrom":makeQuery(id+"F2.opExtrude","SWEPT_FACE",FACE,{"disambiguationData":[OSD([subQ2]),TDD([makeQuery(id+"F0.imprint","IMPRINT",EDGE,{"disambiguationData":[TD([[makeQuery(id+"F0.imprint","INTERSECT",VERTEX,{"derivedFrom":[sQuery(id+"F0.wireOp",EDGE,"E0.top"),subQ2]}),1.0]])],"derivedFrom":subQ2})])]})}),makeQuery(id+"F3.opExtrude","SWEPT_FACE",FACE,{"disambiguationData":[OSD([subQ2])]})]}),makeQuery(id+"F6.opExtrude","CAP_FACE",FACE,{"disambiguationData":[OSD([subQ1,subQ0,sQuery(id+"F0.wireOp",EDGE,"E11.left"),sQuery(id+"F0.wireOp",EDGE,"E11.right")])],"isStart":true})]});}
            var Q8;
            Q8=makeQuery(id+"F2.boolean.opBoolean","COPY",EDGE,{"derivedFrom":makeQuery(id+"F2.opExtrude","CAP_EDGE",EDGE,{"disambiguationData":[OSD([sQuery(id+"F0.wireOp",EDGE,"E3")])],"isStart":false})});
            var Q9;
            Q9=makeQuery(id+"F2.boolean.opBoolean","COPY",EDGE,{"derivedFrom":makeQuery(id+"F2.opExtrude","CAP_EDGE",EDGE,{"disambiguationData":[OSD([sQuery(id+"F0.wireOp",EDGE,"E4")])],"isStart":false})});
            var Q10;
            {var subQ0=sQuery(id+"F0.wireOp",EDGE,"E7");Q10=makeQuery(id+"F2.boolean.opBoolean","COPY",EDGE,{"derivedFrom":makeQuery(id+"F2.opExtrude","CAP_EDGE",EDGE,{"disambiguationData":[OSD([subQ0]),TDD([makeQuery(id+"F0.imprint","IMPRINT",EDGE,{"disambiguationData":[TD([[makeQuery(id+"F0.imprint","INTERSECT",VERTEX,{"disambiguationData":[OD(0.0)],"derivedFrom":[sQuery(id+"F0.wireOp",EDGE,"E0.left"),subQ0]}),1.0]])],"derivedFrom":subQ0})])],"isStart":false})});}
            var Q11;
            Q11=makeQuery(id+"F2.boolean.opBoolean","COPY",EDGE,{"derivedFrom":makeQuery(id+"F2.opExtrude","CAP_EDGE",EDGE,{"disambiguationData":[OSD([sQuery(id+"F0.wireOp",EDGE,"E8")])],"isStart":false})});
            var Q12;
            Q12=makeQuery(id+"F2.boolean.opBoolean","COPY",FACE,{"derivedFrom":makeQuery(id+"F2.opExtrude","CAP_FACE",FACE,{"disambiguationData":[OSD([sQuery(id+"F0.wireOp",EDGE,"E0.bottom"),sQuery(id+"F0.wireOp",EDGE,"E0.left"),sQuery(id+"F0.wireOp",EDGE,"E0.right"),sQuery(id+"F0.wireOp",EDGE,"E3"),sQuery(id+"F0.wireOp",EDGE,"E4"),sQuery(id+"F0.wireOp",EDGE,"E7"),sQuery(id+"F0.wireOp",EDGE,"E8"),sQuery(id+"F0.wireOp",EDGE,"2mZLKPwa-GTBg-M3pd-c2KF-U8wC3PhsdAiK.top")])],"isStart":true})});
            var Q13;
            {var subQ0=sQuery(id+"F0.wireOp",EDGE,"E9.right");Q13=makeQuery(id+"F7.opExtrude","CAP_EDGE",EDGE,{"disambiguationData":[OSD([subQ0]),TDD([makeQuery(id+"F0.imprint","IMPRINT",EDGE,{"disambiguationData":[TD([[makeQuery(id+"F0.imprint","INTERSECT",VERTEX,{"derivedFrom":[subQ0,sQuery(id+"F0.wireOp",EDGE,"E22")]}),-1.0]])],"derivedFrom":subQ0})])],"isStart":false});}
            var Q14;
            {var subQ0=sQuery(id+"F0.wireOp",EDGE,"E9.right");Q14=makeQuery(id+"F7.opExtrude","CAP_EDGE",EDGE,{"disambiguationData":[OSD([subQ0]),TDD([makeQuery(id+"F0.imprint","IMPRINT",EDGE,{"disambiguationData":[TD([[makeQuery(id+"F0.imprint","INTERSECT",VERTEX,{"derivedFrom":[subQ0,sQuery(id+"F0.wireOp",EDGE,"E15")]}),1.0]])],"derivedFrom":subQ0})])],"isStart":false});}
            var Q15;
            {var subQ0=sQuery(id+"F0.wireOp",EDGE,"E9.left");Q15=makeQuery(id+"F7.opExtrude","CAP_EDGE",EDGE,{"disambiguationData":[OSD([subQ0]),TDD([makeQuery(id+"F0.imprint","IMPRINT",EDGE,{"disambiguationData":[TD([[makeQuery(id+"F0.imprint","INTERSECT",VERTEX,{"derivedFrom":[subQ0,sQuery(id+"F0.wireOp",EDGE,"E19")]}),1.0]])],"derivedFrom":subQ0})])],"isStart":false});}
            var Q16;
            {var subQ0=sQuery(id+"F0.wireOp",EDGE,"E9.left");Q16=makeQuery(id+"F7.opExtrude","CAP_EDGE",EDGE,{"disambiguationData":[OSD([subQ0]),TDD([makeQuery(id+"F0.imprint","IMPRINT",EDGE,{"disambiguationData":[TD([[makeQuery(id+"F0.imprint","INTERSECT",VERTEX,{"derivedFrom":[subQ0,sQuery(id+"F0.wireOp",EDGE,"E25")]}),-1.0]])],"derivedFrom":subQ0})])],"isStart":false});}
            var Q17;
            Q17=makeQuery(id+"F1.opExtrude","SWEPT_EDGE",EDGE,{"disambiguationData":[OSD([sQuery(id+"F0.wireOp",EDGE,"E9.top"),sQuery(id+"F0.wireOp",EDGE,"E9.right"),sQuery(id+"F0.wireOp",EDGE,"E20")])]});
            var Q18;
            Q18=makeQuery(id+"F1.opExtrude","SWEPT_EDGE",EDGE,{"disambiguationData":[OSD([sQuery(id+"F0.wireOp",EDGE,"E9.top"),sQuery(id+"F0.wireOp",EDGE,"E9.left"),sQuery(id+"F0.wireOp",EDGE,"E23")])]});
            var Q19;
            Q19=makeQuery(id+"F1.opExtrude","SWEPT_EDGE",EDGE,{"disambiguationData":[OSD([sQuery(id+"F0.wireOp",EDGE,"E9.bottom"),sQuery(id+"F0.wireOp",EDGE,"E9.left"),sQuery(id+"F0.wireOp",EDGE,"E17")])]});
            var Q20;
            Q20=makeQuery(id+"F1.opExtrude","SWEPT_EDGE",EDGE,{"disambiguationData":[OSD([sQuery(id+"F0.wireOp",EDGE,"E9.bottom"),sQuery(id+"F0.wireOp",EDGE,"E9.right"),sQuery(id+"F0.wireOp",EDGE,"E13")])]});
            var Q21;
            {var subQ0=sQuery(id+"F0.wireOp",EDGE,"E9.right");var subQ1=sQuery(id+"F0.wireOp",EDGE,"E9.left");Q21=makeQuery(id+"F7.boolean.opBoolean","MERGE",FACE,{"derivedFrom":[makeQuery(id+"F1.opExtrude","CAP_FACE",FACE,{"disambiguationData":[OSD([sQuery(id+"F0.wireOp",EDGE,"E9.bottom"),sQuery(id+"F0.wireOp",EDGE,"E9.top"),subQ1,subQ0])],"isStart":true}),makeQuery(id+"F7.opExtrude","CAP_FACE",FACE,{"disambiguationData":[OSD([subQ1,sQuery(id+"F0.wireOp",EDGE,"E17"),sQuery(id+"F0.wireOp",EDGE,"E18"),sQuery(id+"F0.wireOp",EDGE,"E19"),sQuery(id+"F0.wireOp",EDGE,"E26")])],"isStart":true}),makeQuery(id+"F7.opExtrude","CAP_FACE",FACE,{"disambiguationData":[OSD([subQ1,sQuery(id+"F0.wireOp",EDGE,"E23"),sQuery(id+"F0.wireOp",EDGE,"E24"),sQuery(id+"F0.wireOp",EDGE,"E25"),sQuery(id+"F0.wireOp",EDGE,"E27")])],"isStart":true}),makeQuery(id+"F7.opExtrude","CAP_FACE",FACE,{"disambiguationData":[OSD([subQ0,sQuery(id+"F0.wireOp",EDGE,"E13"),sQuery(id+"F0.wireOp",EDGE,"E14"),sQuery(id+"F0.wireOp",EDGE,"E15"),sQuery(id+"F0.wireOp",EDGE,"E16")])],"isStart":true}),makeQuery(id+"F7.opExtrude","CAP_FACE",FACE,{"disambiguationData":[OSD([subQ0,sQuery(id+"F0.wireOp",EDGE,"E20"),sQuery(id+"F0.wireOp",EDGE,"E21"),sQuery(id+"F0.wireOp",EDGE,"E22"),sQuery(id+"F0.wireOp",EDGE,"E28")])],"isStart":true})]});}
            var Q22;
            Q22=makeQuery(id+"F7.opExtrude","CAP_FACE",FACE,{"disambiguationData":[OSD([sQuery(id+"F0.wireOp",EDGE,"E9.right"),sQuery(id+"F0.wireOp",EDGE,"E20"),sQuery(id+"F0.wireOp",EDGE,"E21"),sQuery(id+"F0.wireOp",EDGE,"E22"),sQuery(id+"F0.wireOp",EDGE,"E28")])],"isStart":false});
            var Q23;
            Q23=makeQuery(id+"F7.opExtrude","CAP_FACE",FACE,{"disambiguationData":[OSD([sQuery(id+"F0.wireOp",EDGE,"E9.left"),sQuery(id+"F0.wireOp",EDGE,"E23"),sQuery(id+"F0.wireOp",EDGE,"E24"),sQuery(id+"F0.wireOp",EDGE,"E25"),sQuery(id+"F0.wireOp",EDGE,"E27")])],"isStart":false});
            var Q24;
            Q24=makeQuery(id+"F7.opExtrude","CAP_FACE",FACE,{"disambiguationData":[OSD([sQuery(id+"F0.wireOp",EDGE,"E9.left"),sQuery(id+"F0.wireOp",EDGE,"E17"),sQuery(id+"F0.wireOp",EDGE,"E18"),sQuery(id+"F0.wireOp",EDGE,"E19"),sQuery(id+"F0.wireOp",EDGE,"E26")])],"isStart":false});
            var Q25;
            Q25=makeQuery(id+"F7.opExtrude","CAP_FACE",FACE,{"disambiguationData":[OSD([sQuery(id+"F0.wireOp",EDGE,"E9.right"),sQuery(id+"F0.wireOp",EDGE,"E13"),sQuery(id+"F0.wireOp",EDGE,"E14"),sQuery(id+"F0.wireOp",EDGE,"E15"),sQuery(id+"F0.wireOp",EDGE,"E16")])],"isStart":false});
            var Q26;
            Q26=makeQuery(id+"F3.boolean.opBoolean","COPY",EDGE,{"derivedFrom":makeQuery(id+"F3.opExtrude","CAP_EDGE",EDGE,{"disambiguationData":[OSD([sQuery(id+"F0.wireOp",EDGE,"E0.bottom")])],"isStart":false})});
            var Q27;
            Q27=makeQuery(id+"F3.boolean.opBoolean","COPY",EDGE,{"derivedFrom":makeQuery(id+"F3.opExtrude","CAP_EDGE",EDGE,{"disambiguationData":[OSD([sQuery(id+"F0.wireOp",EDGE,"E0.right")])],"isStart":false})});
            var Q28;
            Q28=makeQuery(id+"F3.boolean.opBoolean","COPY",EDGE,{"derivedFrom":makeQuery(id+"F3.opExtrude","CAP_EDGE",EDGE,{"disambiguationData":[OSD([sQuery(id+"F0.wireOp",EDGE,"E0.left")])],"isStart":false})});
            var Q29;
            {var subQ0=sQuery(id+"F0.wireOp",EDGE,"E0.left");var subQ1=sQuery(id+"F0.wireOp",EDGE,"E0.top");var subQ3=sQuery(id+"F0.wireOp",EDGE,"2mZLKPwa-GTBg-M3pd-c2KF-U8wC3PhsdAiK.top");Q29=makeQuery(id+"F5.boolean.opBoolean","SPLIT",EDGE,{"disambiguationData":[TD([makeQuery(id+"F3.opExtrude","SWEPT_FACE",FACE,{"disambiguationData":[OSD([subQ0])]})])],"derivedFrom":makeQuery(id+"F3.boolean.opBoolean","COPY",EDGE,{"derivedFrom":makeQuery(id+"F3.opExtrude","CAP_EDGE",EDGE,{"disambiguationData":[OSD([subQ1,subQ3])],"isStart":false})})});}
            var Q30;
            {var subQ0=sQuery(id+"F0.wireOp",EDGE,"2mZLKPwa-GTBg-M3pd-c2KF-U8wC3PhsdAiK.top");var subQ1=sQuery(id+"F0.wireOp",EDGE,"E0.right");var subQ2=sQuery(id+"F0.wireOp",EDGE,"E0.top");Q30=makeQuery(id+"F5.boolean.opBoolean","SPLIT",EDGE,{"disambiguationData":[TD([makeQuery(id+"F2.boolean.opBoolean","COPY",FACE,{"derivedFrom":makeQuery(id+"F2.opExtrude","SWEPT_FACE",FACE,{"disambiguationData":[OSD([subQ1])]})})])],"derivedFrom":makeQuery(id+"F3.boolean.opBoolean","COPY",EDGE,{"derivedFrom":makeQuery(id+"F3.opExtrude","CAP_EDGE",EDGE,{"disambiguationData":[OSD([subQ2,subQ0])],"isStart":false})})});}
            var Q31;
            Q31=makeQuery(id+"F4.boolean.opBoolean","INTERSECT",EDGE,{"derivedFrom":[makeQuery(id+"F1.opExtrude","SWEPT_FACE",FACE,{"disambiguationData":[OSD([sQuery(id+"F0.wireOp",EDGE,"E9.top")])]}),makeQuery(id+"F4.opExtrude","CAP_FACE",FACE,{"disambiguationData":[OSD([sQuery(id+"F0.wireOp",EDGE,"2mZLKPwa-GTBg-M3pd-c2KF-U8wC3PhsdAiK.bottom"),sQuery(id+"F0.wireOp",EDGE,"2mZLKPwa-GTBg-M3pd-c2KF-U8wC3PhsdAiK.top"),sQuery(id+"F0.wireOp",EDGE,"2mZLKPwa-GTBg-M3pd-c2KF-U8wC3PhsdAiK.left"),sQuery(id+"F0.wireOp",EDGE,"2mZLKPwa-GTBg-M3pd-c2KF-U8wC3PhsdAiK.right")])],"isStart":true})]});
            var Q32;
            Q32=makeQuery(id+"F4.boolean.opBoolean","INTERSECT",EDGE,{"derivedFrom":[makeQuery(id+"F1.opExtrude","SWEPT_FACE",FACE,{"disambiguationData":[OSD([sQuery(id+"F0.wireOp",EDGE,"E9.top")])]}),makeQuery(id+"F4.opExtrude","SWEPT_FACE",FACE,{"disambiguationData":[OSD([sQuery(id+"F0.wireOp",EDGE,"2mZLKPwa-GTBg-M3pd-c2KF-U8wC3PhsdAiK.right")])]})]});
            var Q33;
            Q33=makeQuery(id+"F4.boolean.opBoolean","INTERSECT",EDGE,{"derivedFrom":[makeQuery(id+"F1.opExtrude","SWEPT_FACE",FACE,{"disambiguationData":[OSD([sQuery(id+"F0.wireOp",EDGE,"E9.top")])]}),makeQuery(id+"F4.opExtrude","SWEPT_FACE",FACE,{"disambiguationData":[OSD([sQuery(id+"F0.wireOp",EDGE,"2mZLKPwa-GTBg-M3pd-c2KF-U8wC3PhsdAiK.left")])]})]});
            chamfer(context, id + "F8", {"entities" : qUnion([Q0, Q1, Q2, Q3, Q4, Q5, Q6, Q7, Q8, Q9, Q10, Q11, Q12, Q13, Q14, Q15, Q16, Q17, Q18, Q19, Q20, Q21, Q22, Q23, Q24, Q25, Q26, Q27, Q28, Q29, Q30, Q31, Q32, Q33]), "width" : 0.5 * mm, "tangentPropagation" : true});
        }
    });
